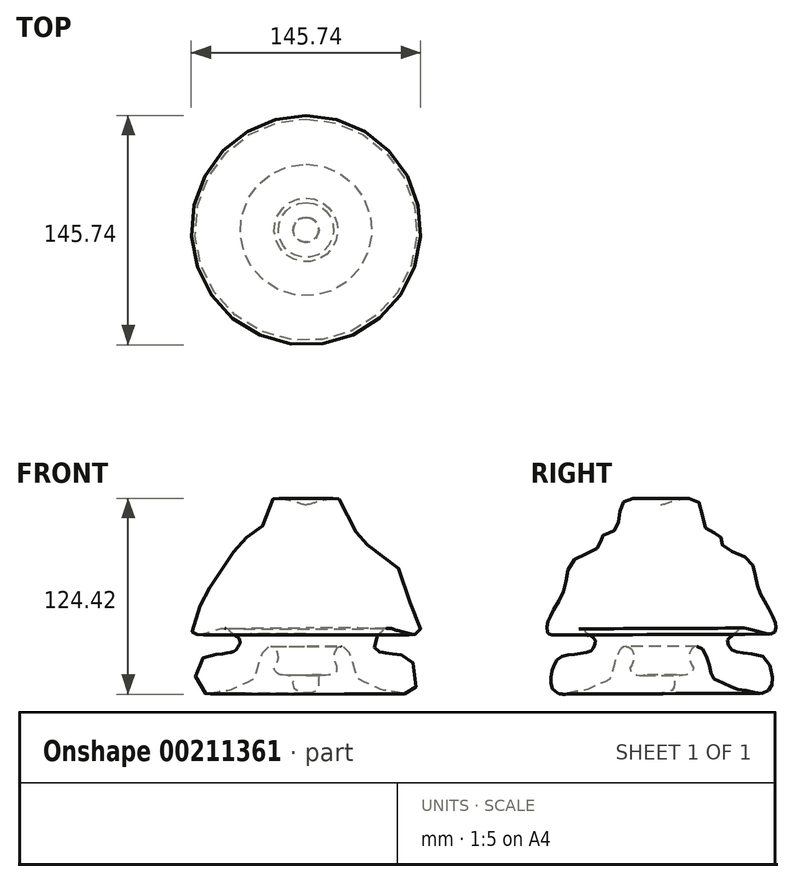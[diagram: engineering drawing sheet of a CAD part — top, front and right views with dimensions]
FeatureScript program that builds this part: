
annotation { "Feature Type Name" : "Feature", "Feature Type Description" : "" }
export const myFeature = defineFeature(function(context is Context, id is Id, definition is map)
    precondition{}
    {
        {
            var Q0;
            Q0=qCreatedBy(makeId("Right.planeOp"),FACE);
            var sketch = newSketch(context, id + "F0", { "sketchPlane" : qUnion([Q0])});
            skFitSpline(sketch, "E0", {"points": [v(0, 52.67) * mm, v(23.76, 54.86) * mm, v(28.76, 37.67) * mm, v(37.5, 33.29) * mm, v(39.39, 27.04) * mm, v(55.01, 18.6) * mm, v(60.33, 7.35) * mm, v(62.52, -2.34) * mm, v(66.27, -8.9) * mm, v(70.64, -17.04) * mm, v(72.83, -22.04) * mm, v(73.14, -24.23) * mm, v(73.14, -26.73) * mm, v(71.58, -28.6) * mm, v(69.7, -29.23) * mm, v(68.46, -29.23) * mm, v(57.2, -26.41) * mm, v(55.64, -25.79) * mm, v(52.83, -25.48) * mm, v(49.39, -26.1) * mm, v(48.76, -27.35) * mm, v(43.14, -31.73) * mm, v(42.51, -35.17) * mm, v(44.07, -37.98) * mm, v(46.26, -40.17) * mm, v(50.01, -40.8) * mm, v(55.01, -41.73) * mm, v(66.27, -44.54) * mm, v(70.96, -57.98) * mm, v(70.33, -62.67) * mm, v(66.9, -66.11) * mm, v(61.58, -66.74) * mm, v(54.7, -65.17) * mm, v(47.82, -64.24) * mm, v(42.82, -61.73) * mm, v(33.76, -57.67) * mm, v(31.88, -53.3) * mm, v(30, -46.42) * mm, v(26.57, -38.92) * mm, v(23.44, -37.04) * mm, v(19.7, -38.6) * mm, v(18.13, -45.17) * mm, v(20.32, -50.17) * mm, v(20.63, -51.73) * mm, v(18.13, -54.55) * mm, v(15.63, -55.17) * mm, v(11.25, -55.48) * mm, v(9.06, -55.48) * mm, v(8.44, -58.6) * mm, v(8.75, -60.48) * mm, v(7.5, -64.55) * mm, v(2.19, -66.74) * mm, v(0, -66.74) * mm], "startDerivative": vector(745.69, 244.75) * mm, "endDerivative": vector(-151.1, 13.51) * mm});
            skLineSegment(sketch, "E1", {"start": v(0, 61.42) * mm, "end": v(0.61, -73.3) * mm});
            skSolve(sketch);
        }
        {
            var Q0;
            {var subQ0=sQuery(id+"F0.wireOp",EDGE,"E1");var subQ1=sQuery(id+"F0.wireOp",EDGE,"E0");var subQ2=makeQuery(id+"F0.imprint","INTERSECT",VERTEX,{"disambiguationData":[OD(0.0)],"derivedFrom":[subQ1,subQ0]});Q0=makeQuery(id+"F0.imprint","IMPRINT",FACE,{"disambiguationData":[TD([[makeQuery(id+"F0.imprint","IMPRINT",EDGE,{"disambiguationData":[TD([[subQ2,1.0]])],"derivedFrom":subQ1}),-1.0]])]});}
            var Q1;
            Q1=sQuery(id+"F0.wireOp",EDGE,"E1");
            revolve(context, id + "F1", {"entities" : qUnion([Q0]), "axis" : qUnion([Q1]), "revolveType" : RevolveType.FULL});
        }
    });
